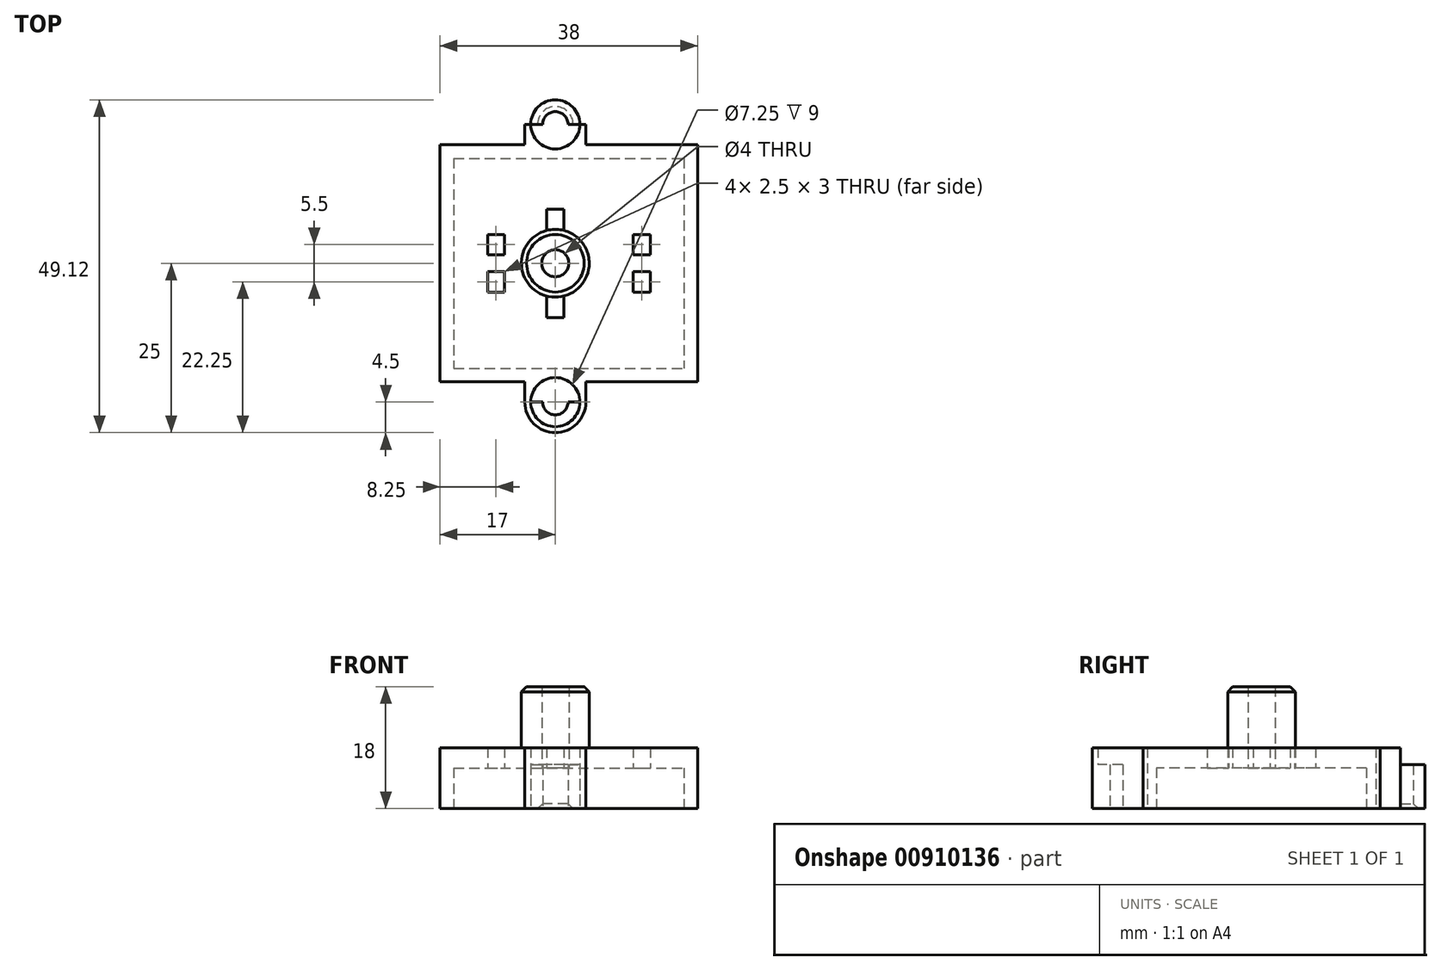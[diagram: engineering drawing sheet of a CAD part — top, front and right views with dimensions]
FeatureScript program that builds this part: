
annotation { "Feature Type Name" : "Feature", "Feature Type Description" : "" }
export const myFeature = defineFeature(function(context is Context, id is Id, definition is map)
    precondition{}
    {
        {
            var Q0;
            Q0=qCreatedBy(makeId("Top.planeOp"),FACE);
            var sketch = newSketch(context, id + "F0", { "sketchPlane" : qUnion([Q0])});
            skCircle(sketch, "E0", {"center": v(0, 0) * mm, "radius": 2 * mm});
            skCircle(sketch, "E1", {"center": v(0, 0) * mm, "radius": 5 * mm});
            skLineSegment(sketch, "E2.bottom", {"start": v(-15, 15.5) * mm, "end": v(19, 15.5) * mm});
            skLineSegment(sketch, "E2.top", {"start": v(-15, -15.5) * mm, "end": v(19, -15.5) * mm});
            skLineSegment(sketch, "E2.left", {"start": v(-15, 15.5) * mm, "end": v(-15, -15.5) * mm});
            skLineSegment(sketch, "E2.right", {"start": v(19, 15.5) * mm, "end": v(19, -15.5) * mm});
            skLineSegment(sketch, "E3.bottom", {"start": v(-17, 17.5) * mm, "end": v(21, 17.5) * mm});
            skLineSegment(sketch, "E3.top", {"start": v(-17, -17.5) * mm, "end": v(21, -17.5) * mm});
            skLineSegment(sketch, "E3.left", {"start": v(-17, 17.5) * mm, "end": v(-17, -17.5) * mm});
            skLineSegment(sketch, "E3.right", {"start": v(21, 17.5) * mm, "end": v(21, -17.5) * mm});
            skLineSegment(sketch, "E4.bottom", {"start": v(-4.5, 17.5) * mm, "end": v(4.5, 17.5) * mm});
            skLineSegment(sketch, "E4.top", {"start": v(-4.5, 20.5) * mm, "end": v(4.5, 20.5) * mm});
            skLineSegment(sketch, "E4.left", {"start": v(-4.5, 17.5) * mm, "end": v(-4.5, 20.5) * mm});
            skLineSegment(sketch, "E4.right", {"start": v(4.5, 17.5) * mm, "end": v(4.5, 20.5) * mm});
            skLineSegment(sketch, "E5.bottom", {"start": v(-4.5, -17.5) * mm, "end": v(4.5, -17.5) * mm});
            skLineSegment(sketch, "E5.top", {"start": v(-4.5, -20.5) * mm, "end": v(4.5, -20.5) * mm});
            skLineSegment(sketch, "E5.left", {"start": v(-4.5, -17.5) * mm, "end": v(-4.5, -20.5) * mm});
            skLineSegment(sketch, "E5.right", {"start": v(4.5, -17.5) * mm, "end": v(4.5, -20.5) * mm});
            skArc(sketch, "E6", {"start": v(-4.5, 20.5) * mm, "mid": v(0, 25) * mm, "end": v(4.5, 20.5) * mm});
            skCircle(sketch, "E7", {"center": v(0, 20.5) * mm, "radius": 3.62 * mm});
            skCircle(sketch, "E8", {"center": v(0, 20.5) * mm, "radius": 1.88 * mm});
            skArc(sketch, "E9", {"start": v(-4.5, -20.5) * mm, "mid": v(0, -25) * mm, "end": v(4.5, -20.5) * mm});
            skCircle(sketch, "E10", {"center": v(0, -20.5) * mm, "radius": 3.62 * mm});
            skCircle(sketch, "E11", {"center": v(0, -20.5) * mm, "radius": 1.88 * mm});
            skLineSegment(sketch, "E12.bottom", {"start": v(-11, 10.5) * mm, "end": v(15, 10.5) * mm});
            skLineSegment(sketch, "E12.top", {"start": v(-11, 8) * mm, "end": v(15, 8) * mm});
            skLineSegment(sketch, "E12.left", {"start": v(-11, 10.5) * mm, "end": v(-11, 8) * mm});
            skLineSegment(sketch, "E12.right", {"start": v(15, 10.5) * mm, "end": v(15, 8) * mm});
            skLineSegment(sketch, "E13.bottom", {"start": v(-11, -8) * mm, "end": v(15, -8) * mm});
            skLineSegment(sketch, "E13.top", {"start": v(-11, -10.5) * mm, "end": v(15, -10.5) * mm});
            skLineSegment(sketch, "E13.left", {"start": v(-11, -8) * mm, "end": v(-11, -10.5) * mm});
            skLineSegment(sketch, "E13.right", {"start": v(15, -8) * mm, "end": v(15, -10.5) * mm});
            skLineSegment(sketch, "E14.bottom", {"start": v(-1.25, -8) * mm, "end": v(1.25, -8) * mm});
            skLineSegment(sketch, "E14.top", {"start": v(-1.25, -2.5) * mm, "end": v(1.25, -2.5) * mm});
            skLineSegment(sketch, "E14.left", {"start": v(-1.25, -8) * mm, "end": v(-1.25, -2.5) * mm});
            skLineSegment(sketch, "E14.right", {"start": v(1.25, -8) * mm, "end": v(1.25, -2.5) * mm});
            skLineSegment(sketch, "E15.bottom", {"start": v(-1.25, 8) * mm, "end": v(1.25, 8) * mm});
            skLineSegment(sketch, "E15.top", {"start": v(-1.25, 2.5) * mm, "end": v(1.25, 2.5) * mm});
            skLineSegment(sketch, "E15.left", {"start": v(-1.25, 8) * mm, "end": v(-1.25, 2.5) * mm});
            skLineSegment(sketch, "E15.right", {"start": v(1.25, 8) * mm, "end": v(1.25, 2.5) * mm});
            skLineSegment(sketch, "E16.bottom", {"start": v(2.5, -1.25) * mm, "end": v(14, -1.25) * mm});
            skLineSegment(sketch, "E16.top", {"start": v(2.5, 1.25) * mm, "end": v(14, 1.25) * mm});
            skLineSegment(sketch, "E16.left", {"start": v(2.5, -1.25) * mm, "end": v(2.5, 1.25) * mm});
            skLineSegment(sketch, "E16.right", {"start": v(14, -1.25) * mm, "end": v(14, 1.25) * mm});
            skLineSegment(sketch, "E17.bottom", {"start": v(-10, -1.25) * mm, "end": v(-2.5, -1.25) * mm});
            skLineSegment(sketch, "E17.top", {"start": v(-10, 1.25) * mm, "end": v(-2.5, 1.25) * mm});
            skLineSegment(sketch, "E17.left", {"start": v(-10, -1.25) * mm, "end": v(-10, 1.25) * mm});
            skLineSegment(sketch, "E17.right", {"start": v(-2.5, -1.25) * mm, "end": v(-2.5, 1.25) * mm});
            skLineSegment(sketch, "E18.bottom", {"start": v(14, -1.25) * mm, "end": v(11.5, -1.25) * mm});
            skLineSegment(sketch, "E18.top", {"start": v(14, -4.25) * mm, "end": v(11.5, -4.25) * mm});
            skLineSegment(sketch, "E18.left", {"start": v(14, -1.25) * mm, "end": v(14, -4.25) * mm});
            skLineSegment(sketch, "E18.right", {"start": v(11.5, -1.25) * mm, "end": v(11.5, -4.25) * mm});
            skLineSegment(sketch, "E19.bottom", {"start": v(14, 1.25) * mm, "end": v(11.5, 1.25) * mm});
            skLineSegment(sketch, "E19.top", {"start": v(14, 4.25) * mm, "end": v(11.5, 4.25) * mm});
            skLineSegment(sketch, "E19.left", {"start": v(14, 1.25) * mm, "end": v(14, 4.25) * mm});
            skLineSegment(sketch, "E19.right", {"start": v(11.5, 1.25) * mm, "end": v(11.5, 4.25) * mm});
            skLineSegment(sketch, "E20.bottom", {"start": v(-10, 1.25) * mm, "end": v(-7.5, 1.25) * mm});
            skLineSegment(sketch, "E20.top", {"start": v(-10, 4.25) * mm, "end": v(-7.5, 4.25) * mm});
            skLineSegment(sketch, "E20.left", {"start": v(-10, 1.25) * mm, "end": v(-10, 4.25) * mm});
            skLineSegment(sketch, "E20.right", {"start": v(-7.5, 1.25) * mm, "end": v(-7.5, 4.25) * mm});
            skLineSegment(sketch, "E21.bottom", {"start": v(-10, -1.25) * mm, "end": v(-7.5, -1.25) * mm});
            skLineSegment(sketch, "E21.top", {"start": v(-10, -4.25) * mm, "end": v(-7.5, -4.25) * mm});
            skLineSegment(sketch, "E21.left", {"start": v(-10, -1.25) * mm, "end": v(-10, -4.25) * mm});
            skLineSegment(sketch, "E21.right", {"start": v(-7.5, -1.25) * mm, "end": v(-7.5, -4.25) * mm});
            skSolve(sketch);
        }
        {
            var Q0;
            Q0=makeQuery(id+"F0.imprint","IMPRINT",FACE,{"disambiguationData":[TD([[makeQuery(id+"F0.imprint","IMPRINT",EDGE,{"derivedFrom":sQuery(id+"F0.wireOp",EDGE,"E2.bottom")}),1.0]])]});
            var Q1;
            {var subQ0=sQuery(id+"F0.wireOp",EDGE,"E4.left");Q1=makeQuery(id+"F0.imprint","IMPRINT",FACE,{"disambiguationData":[TD([[makeQuery(id+"F0.imprint","IMPRINT",EDGE,{"derivedFrom":subQ0}),-1.0]])]});}
            var Q2;
            {var subQ0=sQuery(id+"F0.wireOp",EDGE,"E6");Q2=makeQuery(id+"F0.imprint","IMPRINT",FACE,{"disambiguationData":[TD([[makeQuery(id+"F0.imprint","IMPRINT",EDGE,{"derivedFrom":subQ0}),-1.0]])]});}
            var Q3;
            {var subQ0=sQuery(id+"F0.wireOp",EDGE,"E4.right");Q3=makeQuery(id+"F0.imprint","IMPRINT",FACE,{"disambiguationData":[TD([[makeQuery(id+"F0.imprint","IMPRINT",EDGE,{"derivedFrom":subQ0}),1.0]])]});}
            var Q4;
            {var subQ0=sQuery(id+"F0.wireOp",EDGE,"E5.right");Q4=makeQuery(id+"F0.imprint","IMPRINT",FACE,{"disambiguationData":[TD([[makeQuery(id+"F0.imprint","IMPRINT",EDGE,{"derivedFrom":subQ0}),-1.0]])]});}
            var Q5;
            {var subQ0=sQuery(id+"F0.wireOp",EDGE,"E5.left");Q5=makeQuery(id+"F0.imprint","IMPRINT",FACE,{"disambiguationData":[TD([[makeQuery(id+"F0.imprint","IMPRINT",EDGE,{"derivedFrom":subQ0}),1.0]])]});}
            var Q6;
            {var subQ0=sQuery(id+"F0.wireOp",EDGE,"E9");Q6=makeQuery(id+"F0.imprint","IMPRINT",FACE,{"disambiguationData":[TD([[makeQuery(id+"F0.imprint","IMPRINT",EDGE,{"derivedFrom":subQ0}),1.0]])]});}
            extrude(context, id + "F1", {"entities" : qUnion([Q0, Q1, Q2, Q3, Q4, Q5, Q6]), "depth" : 9 * mm, "offsetDistance" : 25 * mm});
        }
        {
            var Q0;
            {var subQ0=sQuery(id+"F0.wireOp",EDGE,"E7");var subQ1=sQuery(id+"F0.wireOp",EDGE,"E4.bottom");var subQ2=makeQuery(id+"F0.imprint","INTERSECT",VERTEX,{"disambiguationData":[OD(0.0)],"derivedFrom":[subQ1,subQ0]});Q0=makeQuery(id+"F0.imprint","IMPRINT",FACE,{"disambiguationData":[TD([[makeQuery(id+"F0.imprint","IMPRINT",EDGE,{"disambiguationData":[TD([[subQ2,-1.0]])],"derivedFrom":subQ1}),1.0]])]});}
            var Q1;
            {var subQ0=sQuery(id+"F0.wireOp",EDGE,"E7");var subQ1=sQuery(id+"F0.wireOp",EDGE,"E4.bottom");var subQ2=makeQuery(id+"F0.imprint","INTERSECT",VERTEX,{"disambiguationData":[OD(0.0)],"derivedFrom":[subQ1,subQ0]});Q1=makeQuery(id+"F0.imprint","IMPRINT",FACE,{"disambiguationData":[TD([[makeQuery(id+"F0.imprint","IMPRINT",EDGE,{"disambiguationData":[TD([[subQ2,-1.0]])],"derivedFrom":subQ1}),-1.0]])]});}
            var Q2;
            {var subQ0=sQuery(id+"F0.wireOp",EDGE,"E7");var subQ1=sQuery(id+"F0.wireOp",EDGE,"E4.top");var subQ2=makeQuery(id+"F0.imprint","INTERSECT",VERTEX,{"disambiguationData":[OD(0.0)],"derivedFrom":[subQ1,subQ0]});Q2=makeQuery(id+"F0.imprint","IMPRINT",FACE,{"disambiguationData":[TD([[makeQuery(id+"F0.imprint","IMPRINT",EDGE,{"disambiguationData":[TD([[subQ2,-1.0]])],"derivedFrom":subQ1}),1.0]])]});}
            var Q3;
            {var subQ0=sQuery(id+"F0.wireOp",EDGE,"E10");var subQ1=sQuery(id+"F0.wireOp",EDGE,"E5.bottom");var subQ9=makeQuery(id+"F0.imprint","INTERSECT",VERTEX,{"disambiguationData":[OD(0.0)],"derivedFrom":[subQ1,subQ0]});Q3=makeQuery(id+"F0.imprint","IMPRINT",FACE,{"disambiguationData":[TD([[makeQuery(id+"F0.imprint","IMPRINT",EDGE,{"disambiguationData":[TD([[subQ9,-1.0]])],"derivedFrom":subQ1}),-1.0]])]});}
            var Q4;
            {var subQ0=sQuery(id+"F0.wireOp",EDGE,"E10");var subQ1=sQuery(id+"F0.wireOp",EDGE,"E5.bottom");var subQ2=makeQuery(id+"F0.imprint","INTERSECT",VERTEX,{"disambiguationData":[OD(0.0)],"derivedFrom":[subQ1,subQ0]});Q4=makeQuery(id+"F0.imprint","IMPRINT",FACE,{"disambiguationData":[TD([[makeQuery(id+"F0.imprint","IMPRINT",EDGE,{"disambiguationData":[TD([[subQ2,-1.0]])],"derivedFrom":subQ1}),1.0]])]});}
            var Q5;
            {var subQ0=sQuery(id+"F0.wireOp",EDGE,"E10");var subQ1=sQuery(id+"F0.wireOp",EDGE,"E5.top");var subQ2=makeQuery(id+"F0.imprint","INTERSECT",VERTEX,{"disambiguationData":[OD(0.0)],"derivedFrom":[subQ1,subQ0]});Q5=makeQuery(id+"F0.imprint","IMPRINT",FACE,{"disambiguationData":[TD([[makeQuery(id+"F0.imprint","IMPRINT",EDGE,{"disambiguationData":[TD([[subQ2,-1.0]])],"derivedFrom":subQ1}),-1.0]])]});}
            extrude(context, id + "F2", {"entities" : qUnion([Q0, Q1, Q2, Q3, Q4, Q5]), "operationType" : NewBodyOperationType.ADD, "depth" : 6.5 * mm, "offsetDistance" : 25 * mm});
        }
        {
            var Q0;
            Q0=makeQuery(id+"F0.imprint","IMPRINT",FACE,{"disambiguationData":[TD([[makeQuery(id+"F0.imprint","IMPRINT",EDGE,{"derivedFrom":sQuery(id+"F0.wireOp",EDGE,"E1")}),-1.0]])]});
            var Q1;
            Q1=makeQuery(id+"F0.imprint","IMPRINT",FACE,{"disambiguationData":[TD([[makeQuery(id+"F0.imprint","IMPRINT",EDGE,{"derivedFrom":sQuery(id+"F0.wireOp",EDGE,"E20.bottom")}),1.0]])]});
            var Q2;
            Q2=makeQuery(id+"F0.imprint","IMPRINT",FACE,{"disambiguationData":[TD([[makeQuery(id+"F0.imprint","IMPRINT",EDGE,{"derivedFrom":sQuery(id+"F0.wireOp",EDGE,"E17.left")}),-1.0]])]});
            var Q3;
            Q3=makeQuery(id+"F0.imprint","IMPRINT",FACE,{"disambiguationData":[TD([[makeQuery(id+"F0.imprint","IMPRINT",EDGE,{"derivedFrom":sQuery(id+"F0.wireOp",EDGE,"E21.bottom")}),-1.0]])]});
            var Q4;
            Q4=makeQuery(id+"F0.imprint","IMPRINT",FACE,{"disambiguationData":[TD([[makeQuery(id+"F0.imprint","IMPRINT",EDGE,{"derivedFrom":sQuery(id+"F0.wireOp",EDGE,"E13.top")}),1.0]])]});
            var Q5;
            {var subQ5=sQuery(id+"F0.wireOp",EDGE,"E14.bottom");Q5=makeQuery(id+"F0.imprint","IMPRINT",FACE,{"disambiguationData":[TD([[makeQuery(id+"F0.imprint","IMPRINT",EDGE,{"derivedFrom":subQ5}),1.0]])]});}
            var Q6;
            Q6=makeQuery(id+"F0.imprint","IMPRINT",FACE,{"disambiguationData":[TD([[makeQuery(id+"F0.imprint","IMPRINT",EDGE,{"derivedFrom":sQuery(id+"F0.wireOp",EDGE,"E18.bottom")}),1.0]])]});
            var Q7;
            Q7=makeQuery(id+"F0.imprint","IMPRINT",FACE,{"disambiguationData":[TD([[makeQuery(id+"F0.imprint","IMPRINT",EDGE,{"derivedFrom":sQuery(id+"F0.wireOp",EDGE,"E19.bottom")}),-1.0]])]});
            var Q8;
            Q8=makeQuery(id+"F0.imprint","IMPRINT",FACE,{"disambiguationData":[TD([[makeQuery(id+"F0.imprint","IMPRINT",EDGE,{"derivedFrom":sQuery(id+"F0.wireOp",EDGE,"E16.right")}),1.0]])]});
            var Q9;
            Q9=makeQuery(id+"F0.imprint","IMPRINT",FACE,{"disambiguationData":[TD([[makeQuery(id+"F0.imprint","IMPRINT",EDGE,{"derivedFrom":sQuery(id+"F0.wireOp",EDGE,"E12.bottom")}),-1.0]])]});
            var Q10;
            {var subQ5=sQuery(id+"F0.wireOp",EDGE,"E15.bottom");Q10=makeQuery(id+"F0.imprint","IMPRINT",FACE,{"disambiguationData":[TD([[makeQuery(id+"F0.imprint","IMPRINT",EDGE,{"derivedFrom":subQ5}),-1.0]])]});}
            extrude(context, id + "F3", {"entities" : qUnion([Q0, Q1, Q2, Q3, Q4, Q5, Q6, Q7, Q8, Q9, Q10]), "operationType" : NewBodyOperationType.ADD, "depth" : 9 * mm, "offsetDistance" : 25 * mm, "hasSecondDirection" : true, "secondDirectionOppositeDirection" : false, "secondDirectionDepth" : 6 * mm});
        }
        {
            var Q0;
            Q0=makeQuery(id+"F0.imprint","IMPRINT",FACE,{"disambiguationData":[TD([[makeQuery(id+"F0.imprint","IMPRINT",EDGE,{"derivedFrom":sQuery(id+"F0.wireOp",EDGE,"E0")}),-1.0]])]});
            var Q1;
            {var subQ5=sQuery(id+"F0.wireOp",EDGE,"E17.right");Q1=makeQuery(id+"F0.imprint","IMPRINT",FACE,{"disambiguationData":[TD([[makeQuery(id+"F0.imprint","IMPRINT",EDGE,{"derivedFrom":subQ5}),1.0]])]});}
            var Q2;
            {var subQ5=sQuery(id+"F0.wireOp",EDGE,"E14.top");Q2=makeQuery(id+"F0.imprint","IMPRINT",FACE,{"disambiguationData":[TD([[makeQuery(id+"F0.imprint","IMPRINT",EDGE,{"derivedFrom":subQ5}),-1.0]])]});}
            var Q3;
            {var subQ5=sQuery(id+"F0.wireOp",EDGE,"E16.left");Q3=makeQuery(id+"F0.imprint","IMPRINT",FACE,{"disambiguationData":[TD([[makeQuery(id+"F0.imprint","IMPRINT",EDGE,{"derivedFrom":subQ5}),-1.0]])]});}
            var Q4;
            {var subQ5=sQuery(id+"F0.wireOp",EDGE,"E15.top");Q4=makeQuery(id+"F0.imprint","IMPRINT",FACE,{"disambiguationData":[TD([[makeQuery(id+"F0.imprint","IMPRINT",EDGE,{"derivedFrom":subQ5}),1.0]])]});}
            extrude(context, id + "F4", {"entities" : qUnion([Q0, Q1, Q2, Q3, Q4]), "operationType" : NewBodyOperationType.ADD, "depth" : 18 * mm, "offsetDistance" : 25 * mm, "hasSecondDirection" : true, "secondDirectionOppositeDirection" : false, "secondDirectionDepth" : 6 * mm});
        }
        {
            var Q0;
            Q0=makeQuery(id+"F4.opExtrude","CAP_EDGE",EDGE,{"disambiguationData":[OSD([sQuery(id+"F0.wireOp",EDGE,"E1")])],"isStart":false});
            chamfer(context, id + "F5", {"entities" : qUnion([Q0]), "width" : 0.75 * mm, "tangentPropagation" : true});
        }
        {
            var Q0;
            Q0=makeQuery(id+"F2.opExtrude","CAP_EDGE",EDGE,{"disambiguationData":[OSD([sQuery(id+"F0.wireOp",EDGE,"E8")])],"isStart":true});
            chamfer(context, id + "F6", {"entities" : qUnion([Q0]), "width" : 0.75 * mm, "tangentPropagation" : true});
        }
    });
